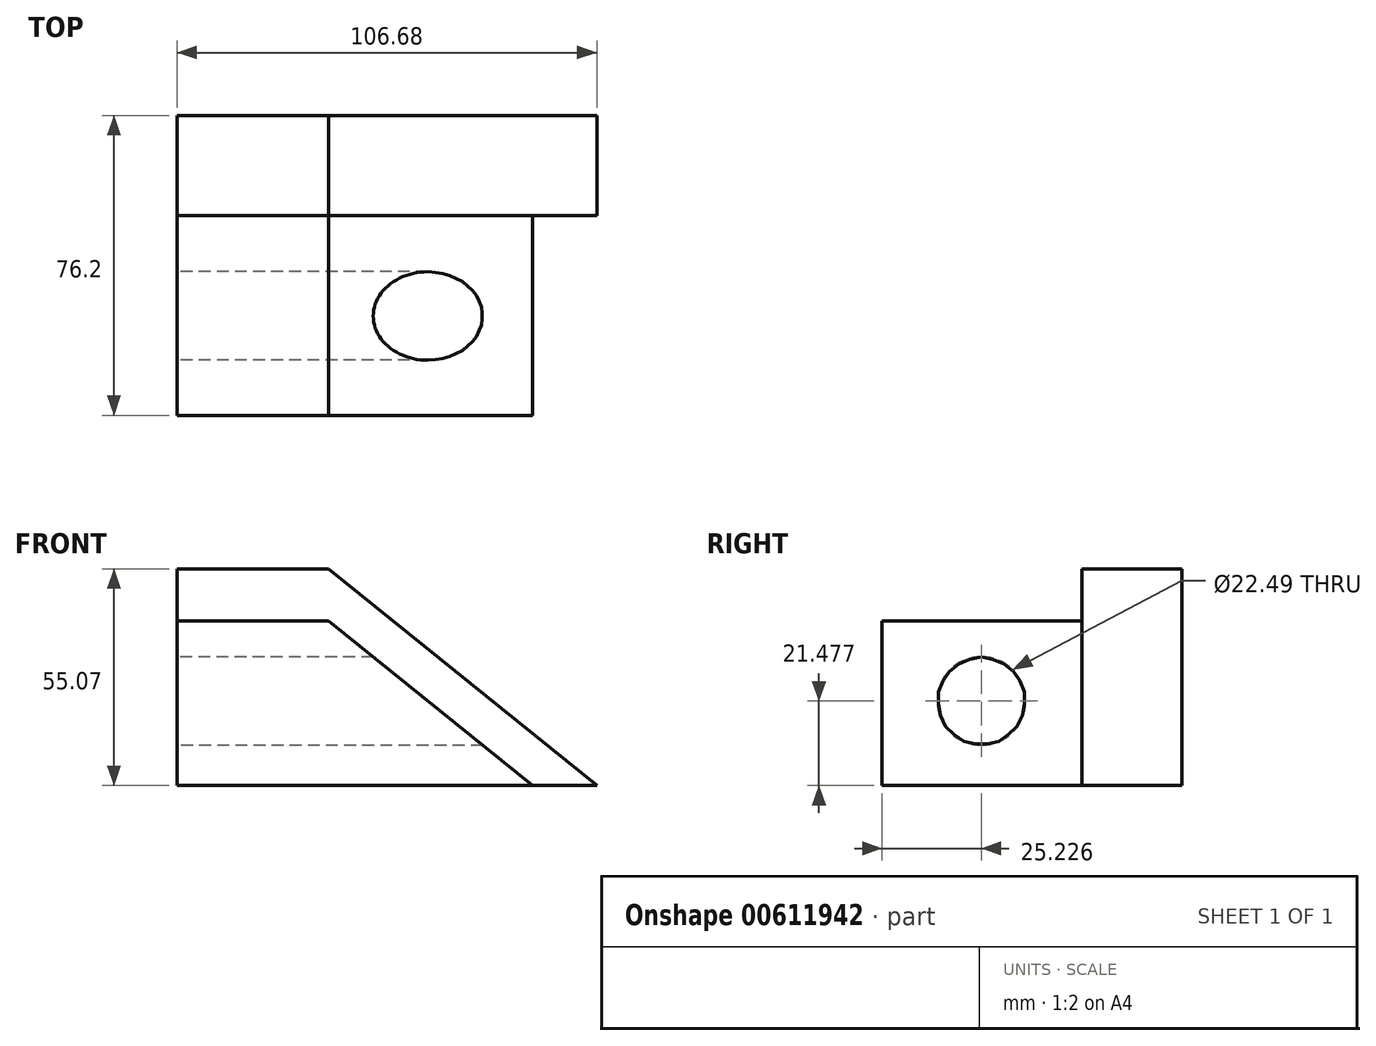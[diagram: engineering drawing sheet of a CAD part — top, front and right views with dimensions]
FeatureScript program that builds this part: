
annotation { "Feature Type Name" : "Feature", "Feature Type Description" : "" }
export const myFeature = defineFeature(function(context is Context, id is Id, definition is map)
    precondition{}
    {
        {
            var Q0;
            Q0=qCreatedBy(makeId("Front.planeOp"),FACE);
            var sketch = newSketch(context, id + "F0", { "sketchPlane" : qUnion([Q0])});
            skLineSegment(sketch, "E0", {"start": v(0, 0) * mm, "end": v(0, 55.07) * mm});
            skLineSegment(sketch, "E1", {"start": v(38.56, 55.07) * mm, "end": v(0, 55.07) * mm});
            skLineSegment(sketch, "E2", {"start": v(38.56, 55.07) * mm, "end": v(106.68, 0) * mm});
            skLineSegment(sketch, "E3", {"start": v(106.68, 0) * mm, "end": v(0, 0) * mm});
            skLineSegment(sketch, "E4", {"start": v(0, 41.86) * mm, "end": v(38.56, 41.86) * mm});
            skLineSegment(sketch, "E5", {"start": v(38.56, 41.86) * mm, "end": v(90.35, 0) * mm});
            skSolve(sketch);
        }
        {
            var Q0;
            {var subQ3=sQuery(id+"F0.wireOp",EDGE,"E4");Q0=makeQuery(id+"F0.imprint","IMPRINT",FACE,{"disambiguationData":[TD([[makeQuery(id+"F0.imprint","IMPRINT",EDGE,{"derivedFrom":subQ3}),-1.0]])]});}
            extrude(context, id + "F1", {"entities" : qUnion([Q0]), "depth" : 76.2 * mm, "offsetDistance" : 25.4 * mm});
        }
        {
            var Q0;
            Q0 = qSketchRegion(id + "F0", true);
            extrude(context, id + "F2", {"entities" : qUnion([Q0]), "operationType" : NewBodyOperationType.ADD, "depth" : 25.4 * mm, "offsetDistance" : 25.4 * mm});
        }
        {
            var Q0;
            Q0=qCreatedBy(makeId("Right.planeOp"),FACE);
            var sketch = newSketch(context, id + "F3", { "sketchPlane" : qUnion([Q0])});
            skCircle(sketch, "E6", {"center": v(-50.97, 21.48) * mm, "radius": 11.25 * mm});
            skSolve(sketch);
        }
        {
            var Q0;
            Q0 = qSketchRegion(id + "F3", true);
            extrude(context, id + "F4", {"entities" : qUnion([Q0]), "operationType" : NewBodyOperationType.REMOVE, "depth" : 152.4 * mm, "offsetDistance" : 25.4 * mm});
        }
    });
